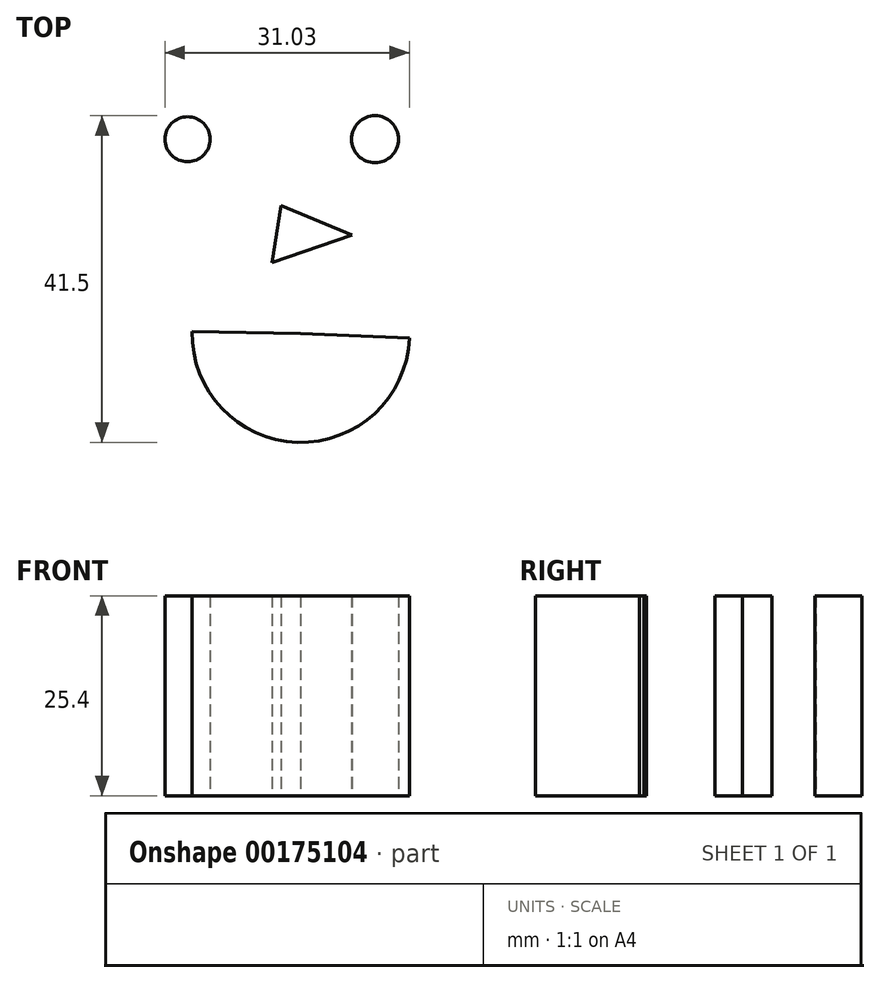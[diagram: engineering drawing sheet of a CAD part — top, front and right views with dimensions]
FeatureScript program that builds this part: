
annotation { "Feature Type Name" : "Feature", "Feature Type Description" : "" }
export const myFeature = defineFeature(function(context is Context, id is Id, definition is map)
    precondition{}
    {
        {
            var Q0;
            Q0=qCreatedBy(makeId("Top.planeOp"),FACE);
            var sketch = newSketch(context, id + "F0", { "sketchPlane" : qUnion([Q0])});
            skCircle(sketch, "E0", {"center": v(-52.86, 43.7) * mm, "radius": 2.86 * mm});
            skCircle(sketch, "E1", {"center": v(-29.04, 43.7) * mm, "radius": 3 * mm});
            skLineSegment(sketch, "E2", {"start": v(-40.95, 35.29) * mm, "end": v(-31.95, 31.51) * mm});
            skLineSegment(sketch, "E3", {"start": v(-31.95, 31.51) * mm, "end": v(-42.11, 28.03) * mm});
            skLineSegment(sketch, "E4", {"start": v(-42.11, 28.03) * mm, "end": v(-40.95, 35.29) * mm});
            skArc(sketch, "E5", {"start": v(-52.28, 19.31) * mm, "mid": v(-38.91, 5.2) * mm, "end": v(-24.69, 18.44) * mm});
            skLineSegment(sketch, "E6", {"start": v(-52.28, 19.31) * mm, "end": v(-38.48, 19) * mm});
            skLineSegment(sketch, "E7", {"start": v(-24.69, 18.44) * mm, "end": v(-38.48, 19) * mm});
            skSolve(sketch);
        }
        {
            var Q0;
            Q0 = qSketchRegion(id + "F0", true);
            extrude(context, id + "F1", {"entities" : qUnion([Q0]), "depth" : 25.4 * mm});
        }
    });
